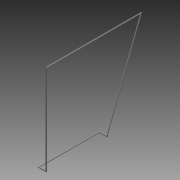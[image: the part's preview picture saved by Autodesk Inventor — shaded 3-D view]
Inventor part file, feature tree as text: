
AUTODESK INVENTOR PART (.ipt)
format: ipt  version: 2013 (Build 170138000, 138)  size: 162,816 bytes
history: native  units: in
note: dims shown in document units (in); Inventor stores cm internally (conversion verified against a paired STEP export)
features: extrude x6, sketch x6, fillet x1
ambient origin geometry x8: Origin, YZ Plane, XZ Plane, XY Plane, X Axis, Y Axis, Z Axis, Center Point
bodies: Solid1 (feature_tree)
feature tree (13):
  extrude  "Extrusion1"  Depth=15.0in
  extrude  "Extrusion2"  Depth=0.25in
  extrude  "Extrusion3"  Depth=1.5in TaperAngle=0.0deg
  extrude  "Extrusion5"  Depth=22.0in
  extrude  "Extrusion6"  Depth=0.25in
  extrude  "Extrusion8"  Depth=14.5in TaperAngle=0.0deg
  fillet  "Fillet4"  Radius=8.5in
  sketch  "Sketch1"  dims[d0=0.25in d1=15.0in]
  sketch  "Sketch2"  dims[d2=0.25in d3=0.0in d4=0.25in]
  sketch  "Sketch3"  dims[d5=0.25in d6=1.5in d7=0.0in]
  sketch  "Sketch5"  dims[d8=0.25in d9=22.0in]
  sketch  "Sketch7"  dims[d10=0.25in d11=0.0in d16=0.25in]
  sketch  "Sketch9"  dims[d17=0.25in d18=14.5in d19=0.0in d21=8.5in d22=0.0in d35=21.75in d36=90.0deg d37=8.5in d38=90.0deg d39=0.25in d40=90.0deg d41=0.25in d42=0.25in d43=0.25in d44=0.0in d45=0.125in]
